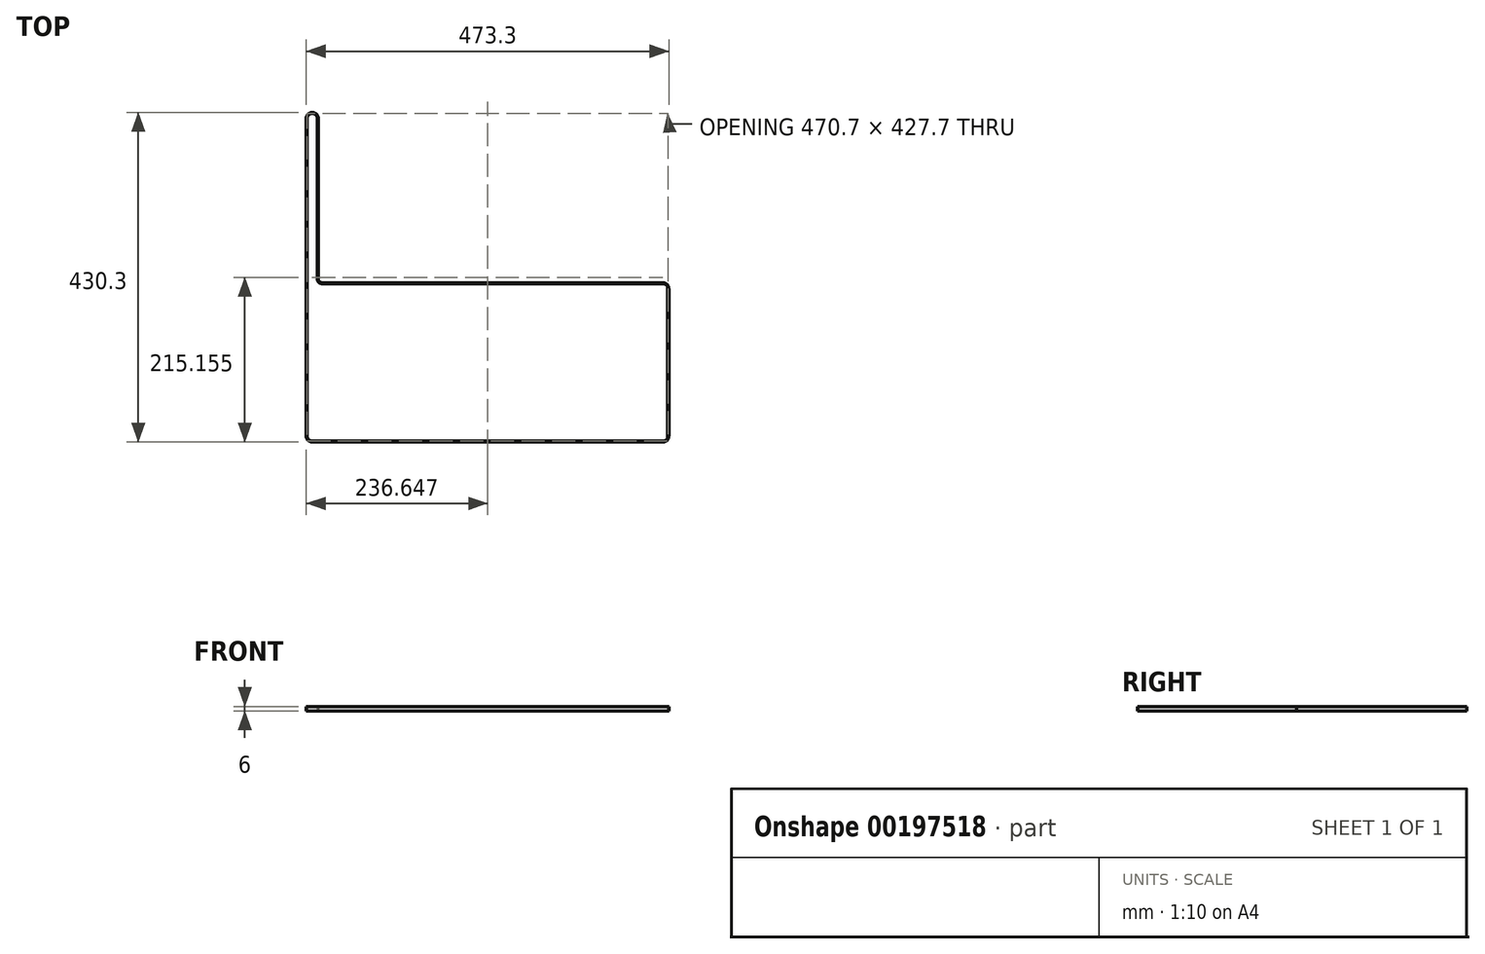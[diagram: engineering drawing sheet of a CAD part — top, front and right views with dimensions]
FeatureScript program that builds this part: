
annotation { "Feature Type Name" : "Feature", "Feature Type Description" : "" }
export const myFeature = defineFeature(function(context is Context, id is Id, definition is map)
    precondition{}
    {
        {
            var Q0;
            Q0=qCreatedBy(makeId("Top.planeOp"),FACE);
            var sketch = newSketch(context, id + "F0", { "sketchPlane" : qUnion([Q0])});
            skArc(sketch, "E0", {"start": v(-188.46, 261.3) * mm, "mid": v(-194.96, 267.8) * mm, "end": v(-201.46, 261.3) * mm});
            skArc(sketch, "E1", {"start": v(-201.46, -153.4) * mm, "mid": v(-199.56, -158) * mm, "end": v(-194.96, -159.9) * mm});
            skArc(sketch, "E2", {"start": v(262.74, -159.9) * mm, "mid": v(267.33, -158) * mm, "end": v(269.24, -153.4) * mm});
            skCircle(sketch, "E3", {"center": v(-194.96, 261.3) * mm, "radius": 2.55 * mm, "construction": true});
            skLineSegment(sketch, "E4", {"start": v(262.74, -159.9) * mm, "end": v(-194.96, -159.9) * mm});
            skLineSegment(sketch, "E5", {"start": v(-201.46, -153.4) * mm, "end": v(-201.46, 261.3) * mm});
            skLineSegment(sketch, "E6", {"start": v(-188.46, 261.3) * mm, "end": v(-188.46, 51.95) * mm});
            skArc(sketch, "E7", {"start": v(-188.46, 51.95) * mm, "mid": v(-186.56, 47.36) * mm, "end": v(-181.96, 45.45) * mm});
            skLineSegment(sketch, "E8", {"start": v(-181.96, 45.45) * mm, "end": v(22.39, 45.45) * mm});
            skArc(sketch, "E9", {"start": v(269.24, 38.95) * mm, "mid": v(267.33, 43.55) * mm, "end": v(262.74, 45.45) * mm});
            skLineSegment(sketch, "E10", {"start": v(269.24, -153.4) * mm, "end": v(269.24, 38.95) * mm});
            skLineSegment(sketch, "E11", {"start": v(22.39, 45.45) * mm, "end": v(262.74, 45.45) * mm});
            skArc(sketch, "E12.0", {"start": v(-187.16, 261.3) * mm, "mid": v(-194.96, 269.1) * mm, "end": v(-202.76, 261.3) * mm});
            skArc(sketch, "E13.0", {"start": v(-187.16, 51.95) * mm, "mid": v(-185.64, 48.28) * mm, "end": v(-181.96, 46.75) * mm});
            skArc(sketch, "E14.0", {"start": v(270.54, 38.95) * mm, "mid": v(268.25, 44.47) * mm, "end": v(262.74, 46.75) * mm});
            skArc(sketch, "E15.0", {"start": v(262.74, -161.2) * mm, "mid": v(268.25, -158.91) * mm, "end": v(270.54, -153.4) * mm});
            skArc(sketch, "E16.0", {"start": v(-202.76, -153.4) * mm, "mid": v(-200.48, -158.91) * mm, "end": v(-194.96, -161.2) * mm});
            skLineSegment(sketch, "E17", {"start": v(-202.76, 261.3) * mm, "end": v(-202.76, -153.4) * mm});
            skLineSegment(sketch, "E18", {"start": v(-194.96, -161.2) * mm, "end": v(262.74, -161.2) * mm});
            skLineSegment(sketch, "E19", {"start": v(270.54, -153.4) * mm, "end": v(270.54, 38.95) * mm});
            skLineSegment(sketch, "E20", {"start": v(262.74, 46.75) * mm, "end": v(-181.96, 46.75) * mm});
            skLineSegment(sketch, "E21", {"start": v(-187.16, 51.95) * mm, "end": v(-187.16, 261.3) * mm});
            skSolve(sketch);
        }
        {
            var Q0;
            Q0=qSketchRegion(id+"F0",true);
            extrude(context, id + "F1", {"entities" : qUnion([Q0]), "depth" : 6 * mm});
        }
    });
